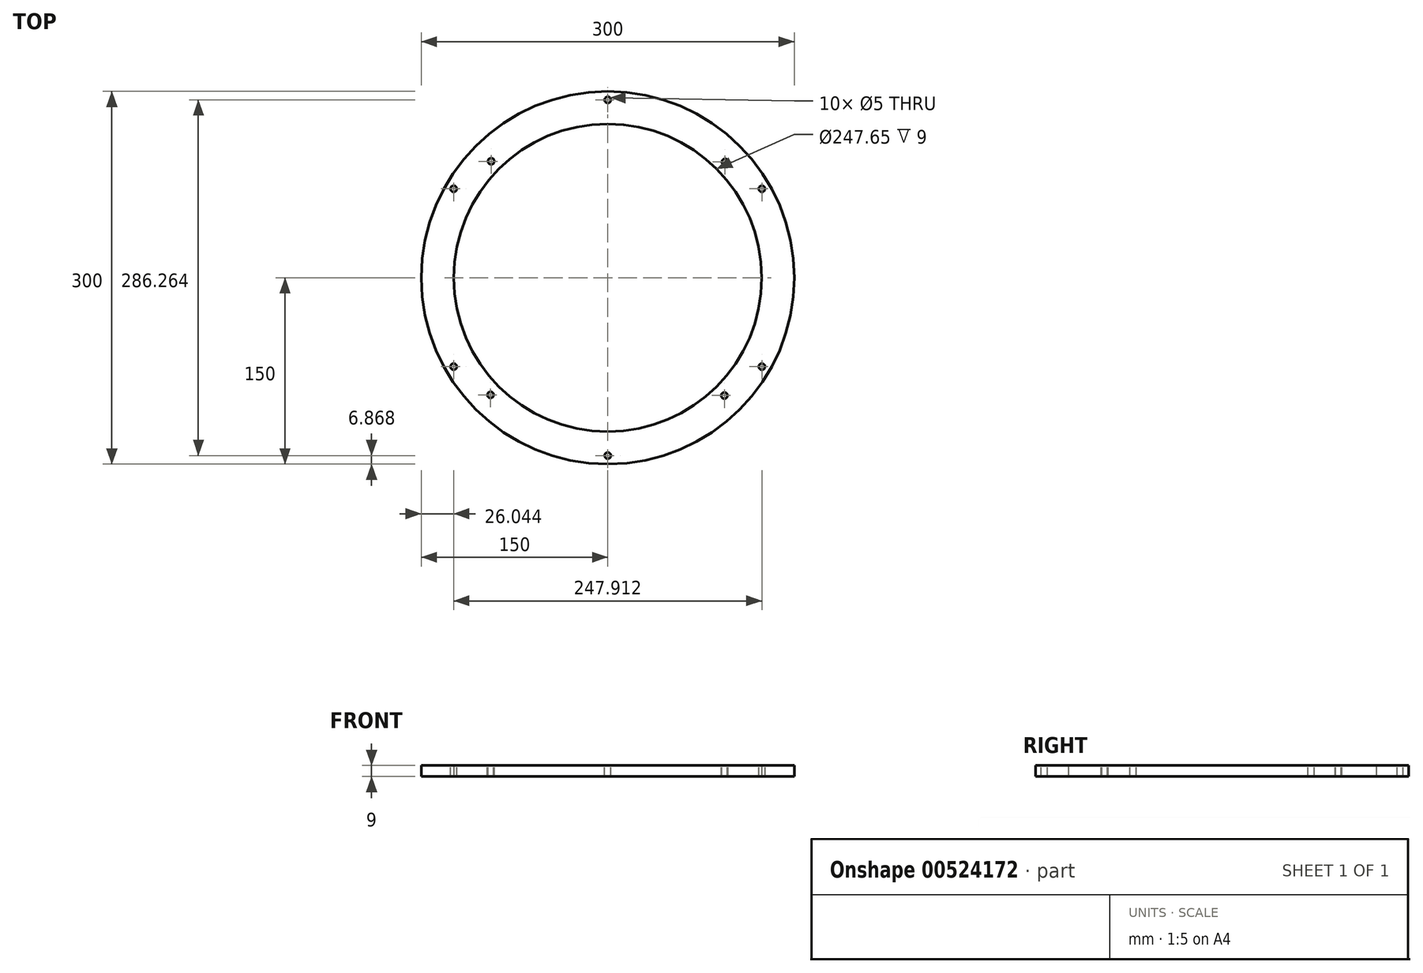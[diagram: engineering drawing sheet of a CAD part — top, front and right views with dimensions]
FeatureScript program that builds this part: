
annotation { "Feature Type Name" : "Feature", "Feature Type Description" : "" }
export const myFeature = defineFeature(function(context is Context, id is Id, definition is map)
    precondition{}
    {
        {
            var Q0;
            Q0=qCreatedBy(makeId("Top.planeOp"),FACE);
            var sketch = newSketch(context, id + "F0", { "sketchPlane" : qUnion([Q0])});
            skCircle(sketch, "E0", {"center": v(0, 0) * mm, "radius": 150 * mm});
            skCircle(sketch, "E1", {"center": v(0, 0) * mm, "radius": 123.83 * mm});
            skSolve(sketch);
        }
        {
            var Q0;
            Q0=makeQuery(id+"F0.imprint","IMPRINT",FACE,{"disambiguationData":[TD([[makeQuery(id+"F0.imprint","IMPRINT",EDGE,{"derivedFrom":sQuery(id+"F0.wireOp",EDGE,"E0")}),1.0]])]});
            extrude(context, id + "F1", {"entities" : qUnion([Q0]), "depth" : 9 * mm});
        }
        {
            var Q0;
            Q0=makeQuery(id+"F1.opExtrude","CAP_FACE",FACE,{"disambiguationData":[OSD([sQuery(id+"F0.wireOp",EDGE,"E0"),sQuery(id+"F0.wireOp",EDGE,"E1")])],"isStart":false});
            var sketch = newSketch(context, id + "F2", { "sketchPlane" : qUnion([Q0])});
            skPoint(sketch, "E2.middle", {"position": v(0, 0) * mm});
            skCircle(sketch, "E3", {"center": v(-94.3, -94.3) * mm, "radius": 2.5 * mm});
            skCircle(sketch, "E4.1.0", {"center": v(93.76, -94.83) * mm, "radius": 2.5 * mm});
            skCircle(sketch, "E4.2.0", {"center": v(94.3, 93.22) * mm, "radius": 2.5 * mm});
            skCircle(sketch, "E4.3.0", {"center": v(-93.76, 93.76) * mm, "radius": 2.5 * mm});
            skPoint(sketch, "E4.center", {"position": v(0, -0.54) * mm});
            skCircle(sketch, "E5", {"center": v(0, 143.13) * mm, "radius": 2.5 * mm});
            skCircle(sketch, "E6.1.0", {"center": v(123.96, 71.57) * mm, "radius": 2.5 * mm});
            skCircle(sketch, "E6.2.0", {"center": v(123.96, -71.57) * mm, "radius": 2.5 * mm});
            skCircle(sketch, "E6.3.0", {"center": v(0, -143.13) * mm, "radius": 2.5 * mm});
            skCircle(sketch, "E6.4.0", {"center": v(-123.96, -71.57) * mm, "radius": 2.5 * mm});
            skCircle(sketch, "E6.5.0", {"center": v(-123.96, 71.57) * mm, "radius": 2.5 * mm});
            skLineSegment(sketch, "E6.anchor1", {"start": v(0, 0) * mm, "end": v(0, 143.13) * mm, "construction": true});
            skLineSegment(sketch, "E6.anchor2", {"start": v(0, 0) * mm, "end": v(-123.96, 71.57) * mm, "construction": true});
            skSolve(sketch);
        }
        {
            var Q0;
            Q0=qSketchRegion(id+"F2",true);
            extrude(context, id + "F3", {"entities" : qUnion([Q0]), "operationType" : NewBodyOperationType.REMOVE, "oppositeDirection" : true, "depth" : 25.4 * mm});
        }
    });
